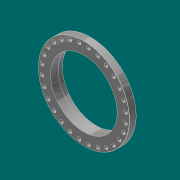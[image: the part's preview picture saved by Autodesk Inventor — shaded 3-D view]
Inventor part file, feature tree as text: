
AUTODESK INVENTOR PART (.ipt)
format: ipt  version: 2017.3 (Build 213257000, 257)  size: 327,168 bytes
history: native  units: in
note: dims shown in document units (in); Inventor stores cm internally (conversion verified against a paired STEP export)
features: sketch x7, extrude x5, chamfer x3, fillet x2, hole x1, pattern_circular x1, revolve x1, projected_geometry x1
ambient origin geometry x8: Origin, YZ Plane, XZ Plane, XY Plane, X Axis, Y Axis, Z Axis, Center Point
bodies: Solid1 (feature_tree)
feature tree (21):
  extrude  "Extrusion1"  Depth=31.0in
  extrude  "Extrusion2"  Depth=3.125in
  extrude  "Extrusion3"  Depth=32.75in
  hole  "Hole1"  [1 undecoded]
  chamfer  "Chamfer3"  Distance=11.0236in Angle=360.0deg
  pattern_circular  "Circular Pattern1"  [2 undecoded]
  chamfer  "Chamfer2"  Distance=0.0312in Angle=45.0deg
  fillet  "Fillet2"  Radius=0.1374in
  revolve  "Revolution3"  [1 undecoded]
  extrude  "Extrusion6"  Depth=0.5in
  extrude  "Extrusion7"  TaperAngle=90.0deg  [1 undecoded]
  fillet  "Fillet5"  Radius=0.2577in
  chamfer  "Chamfer9"  Distance=0.4375in
  sketch  "Sketch1"  dims[d0=41.75in d1=31.0in]
  sketch  "Sketch2"  dims[d2=3.125in d3=0.0in d4=36.0in]
  sketch  "Sketch3"  dims[d5=0.0625in d6=0.0in d7=32.75in]
  sketch  "Sketch4"  dims[d8=2.5in d9=0.0in d13=19.25in]
  sketch  "Sketch9"  dims[d14=0.0442in]
  sketch  "Sketch13"  dims[d15=1.625in d16=0.75in d17=0.375in d18=0.25in d19=0.5635in d20=1.0in d21=0.8108in d22=11.0236in d23=360.0deg]
  projected_geometry  "Projected Loop1"
  sketch  "Sketch14"  dims[d25=0.0625in d26=0.125in d27=0.0687in d29=0.4375in d30=0.0312in d31=0.125in d32=45.0deg d77=0.1374in d78=16.0in d79=0.5in d81=90.0deg d84=0.2577in d85=0.4375in d99=0.625in d119=0.0625in d120=0.0in d121=30.5in d122=3.5in d123=0.0in d124=0.0312in d125=0.0312in d126=0.125in d127=45.0deg]
note: 5 required parameter values undecoded (feature->parameter linkage not recoverable at this tier; creation-order binding heuristic only, values carry confidence <= 0.55)